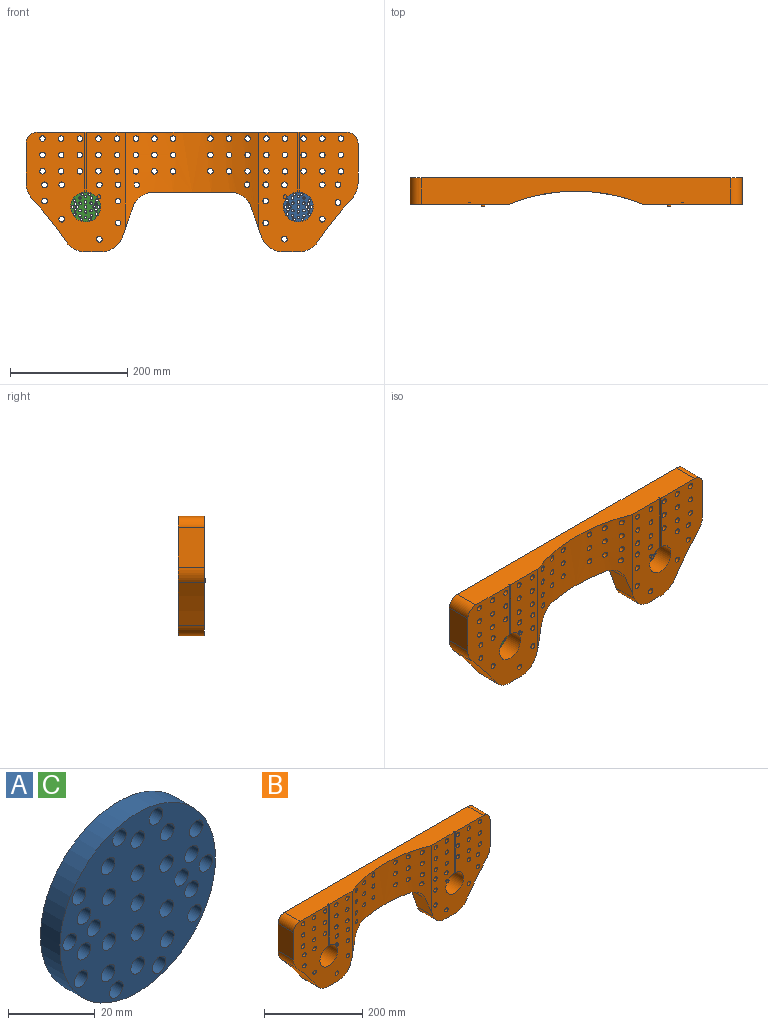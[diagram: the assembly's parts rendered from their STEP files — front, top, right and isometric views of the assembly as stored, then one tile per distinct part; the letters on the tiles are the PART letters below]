
ASSEMBLY  parts=3 mates=2
PART A: 32 faces, bbox 50.8x6.4x50.8 mm
  f0: cylinder r=2.22mm len=6.35mm, axis (0,1,0), area 88.7mm2, adj f30,f31
  f1: cylinder r=2.22mm len=6.35mm, axis (0,1,0), area 88.7mm2, adj f30,f31
  f2: cylinder r=2.22mm len=6.35mm, axis (0,1,0), area 88.7mm2, adj f30,f31
  f3: cylinder r=2.22mm len=6.35mm, axis (0,1,0), area 88.7mm2, adj f30,f31
  f4: cylinder r=2.22mm len=6.35mm, axis (0,1,0), area 88.7mm2, adj f30,f31
  f5: cylinder r=2.22mm len=6.35mm, axis (0,1,0), area 88.7mm2, adj f30,f31
  f6: cylinder r=2.22mm len=6.35mm, axis (0,1,0), area 88.7mm2, adj f30,f31
  f7: cylinder r=2.22mm len=6.35mm, axis (0,1,0), area 88.7mm2, adj f30,f31
  f8: cylinder r=2.22mm len=6.35mm, axis (0,1,0), area 88.7mm2, adj f30,f31
  f9: cylinder r=2.22mm len=6.35mm, axis (0,1,0), area 88.7mm2, adj f30,f31
  f10: cylinder r=2.22mm len=6.35mm, axis (0,1,0), area 88.7mm2, adj f30,f31
  f11: cylinder r=2.22mm len=6.35mm, axis (0,1,0), area 88.7mm2, adj f30,f31
  f12: cylinder r=2.22mm len=6.35mm, axis (0,1,0), area 88.7mm2, adj f30,f31
  f13: cylinder r=2.22mm len=6.35mm, axis (0,1,0), area 88.7mm2, adj f30,f31
  f14: cylinder r=2.22mm len=6.35mm, axis (0,1,0), area 88.7mm2, adj f30,f31
  f15: cylinder r=2.22mm len=6.35mm, axis (0,1,0), area 88.7mm2, adj f30,f31
  f16: cylinder r=2.22mm len=6.35mm, axis (0,1,0), area 88.7mm2, adj f30,f31
  f17: cylinder r=2.22mm len=6.35mm, axis (0,1,0), area 88.7mm2, adj f30,f31
  f18: cylinder r=25.4mm len=50.8mm, axis (0,1,0), area 1013.4mm2, adj f30,f31
  f19: cylinder r=2.22mm len=6.35mm, axis (0,1,0), area 88.7mm2, adj f30,f31
  f20: cylinder r=2.22mm len=6.35mm, axis (0,1,0), area 88.7mm2, adj f30,f31
  f21: cylinder r=2.22mm len=6.35mm, axis (0,1,0), area 88.7mm2, adj f30,f31
  f22: cylinder r=2.22mm len=6.35mm, axis (0,1,0), area 88.7mm2, adj f30,f31
  f23: cylinder r=2.22mm len=6.35mm, axis (0,1,0), area 88.7mm2, adj f30,f31
  f24: cylinder r=2.22mm len=6.35mm, axis (0,1,0), area 88.7mm2, adj f30,f31
  f25: cylinder r=2.22mm len=6.35mm, axis (0,1,0), area 88.7mm2, adj f30,f31
  f26: cylinder r=2.22mm len=6.35mm, axis (0,1,0), area 88.7mm2, adj f30,f31
  f27: cylinder r=2.22mm len=6.35mm, axis (0,1,0), area 88.7mm2, adj f30,f31
  f28: cylinder r=2.22mm len=6.35mm, axis (0,1,0), area 88.7mm2, adj f30,f31
  f29: cylinder r=2.22mm len=6.35mm, axis (0,1,0), area 88.7mm2, adj f30,f31
  f30: plane 50.8x50.8mm, normal (0,-1,0), area 1576.8mm2, adj f0,f1,f2,f3,f4,f5,f6,f7
  f31: plane 50.8x50.8mm, normal (0,1,0), area 1576.8mm2, adj f0,f1,f2,f3,f4,f5,f6,f7
PART B: 110 faces, bbox 565.2x47.6x203.2 mm
  f0: plane 203.2x168.71mm, normal (0,-1,0), area 25330.4mm2, adj f2,f4,f6,f7,f8,f9,f10,f11
  f1: plane 203.2x168.71mm, normal (0,-1,0), area 25330.4mm2, adj f2,f3,f4,f12,f13,f14,f15,f16
  f2: plane 527.05x44.45mm, normal (0,0,1), area 20014.2mm2, adj f0,f1,f4,f5,f11,f12,f98,f99
  f3: cylinder r=25.4mm len=50.8mm, axis (0,1,0), area 6070.4mm2, adj f1,f28,f98,f99,f100,f104
  f4: cylinder r=303.37mm len=227.74mm, axis (0,0,-1), area 24015.6mm2, adj f0,f1,f2,f19,f20,f21,f22,f23
  f5: plane 565.15x203.2mm, normal (0,1,0), area 69669.2mm2, adj f2,f6,f7,f8,f9,f10,f11,f12
  f6: plane 44.45x28.44mm, normal (0,0,-1), area 1264mm2, adj f0,f5,f7,f25
  f7: cylinder r=38.1mm len=44.45mm, axis (0,1,0), area 1651.6mm2, adj f0,f5,f6,f8
  f8: cylinder r=659.08mm len=74.21mm, axis (0,1,0), area 4202.9mm2, adj f0,f5,f7,f9
  f9: cylinder r=38.1mm len=44.45mm, axis (0,1,0), area 1251.6mm2, adj f0,f5,f8,f10
  f10: plane 67.55x44.45mm, normal (1,0,0), area 3002.8mm2, adj f0,f5,f9,f11
  f11: cylinder r=19.05mm len=44.45mm, axis (0,1,0), area 1330.1mm2, adj f0,f2,f5,f10
  f12: cylinder r=19.05mm len=44.45mm, axis (0,1,0), area 1330.1mm2, adj f1,f2,f5,f13
  f13: plane 67.55x44.45mm, normal (-1,0,0), area 3002.8mm2, adj f1,f5,f12,f14
  f14: cylinder r=38.1mm len=44.45mm, axis (0,1,0), area 1251.6mm2, adj f1,f5,f13,f15
  f15: cylinder r=659.08mm len=74.21mm, axis (0,1,0), area 4202.9mm2, adj f1,f5,f14,f16
  f16: cylinder r=38.1mm len=44.45mm, axis (0,1,0), area 1651.6mm2, adj f1,f5,f15,f17
  f17: plane 44.45x28.44mm, normal (0,0,-1), area 1264mm2, adj f1,f5,f16,f18
  f18: cylinder r=38.1mm len=44.45mm, axis (0,1,0), area 2099.5mm2, adj f1,f5,f17,f19
  f19: plane 50.17x44.45mm, normal (0.95,0,-0.33), area 2258.2mm2, adj f1,f4,f5,f18,f20
  f20: cylinder r=38.1mm len=39.55mm, axis (0,1,0), area 1644.6mm2, adj f4,f5,f19,f21
  f21: plane 129.77x29.29mm, normal (0,0,-1), area 3192mm2, adj f4,f5,f20,f22
  f22: cylinder r=38.1mm len=39.55mm, axis (0,1,0), area 1644.6mm2, adj f4,f5,f21,f23
  f23: plane 50.17x44.45mm, normal (-0.95,0,-0.33), area 2258.2mm2, adj f0,f4,f5,f22,f25
  f24: cylinder r=25.4mm len=50.8mm, axis (0,1,0), area 6070.4mm2, adj f0,f27,f101,f102,f103,f107
  f25: cylinder r=38.1mm len=44.45mm, axis (0,1,0), area 2099.5mm2, adj f0,f5,f6,f23
  f26: cylinder r=38.1mm len=76.2mm, axis (0,1,0), area 1520.1mm2, adj f5,f27
  f27: plane 76.2x76.2mm, normal (0,1,0), area 2533.5mm2, adj f24,f26
  f28: plane 76.2x76.2mm, normal (0,1,0), area 2533.5mm2, adj f3,f29
  f29: cylinder r=38.1mm len=76.2mm, axis (0,1,0), area 1520.1mm2, adj f5,f28
  f30: cylinder r=4.76mm len=24.42mm, axis (0,1,0), area 715.4mm2, adj f4,f5
  f31: cylinder r=4.76mm len=24.53mm, axis (0,1,0), area 718.2mm2, adj f4,f5
  f32: cylinder r=4.76mm len=29.94mm, axis (0,1,0), area 865.1mm2, adj f4,f5
  f33: cylinder r=4.76mm len=24.42mm, axis (0,1,0), area 715.4mm2, adj f4,f5
  f34: cylinder r=4.76mm len=24.53mm, axis (0,1,0), area 718.2mm2, adj f4,f5
  f35: cylinder r=4.76mm len=24.53mm, axis (0,1,0), area 718.2mm2, adj f4,f5
  f36: cylinder r=4.76mm len=24.42mm, axis (0,1,0), area 715.4mm2, adj f4,f5
  f37: cylinder r=4.76mm len=29.94mm, axis (0,1,0), area 865.1mm2, adj f4,f5
  f38: cylinder r=4.76mm len=30.16mm, axis (0,1,0), area 871mm2, adj f4,f5
  f39: cylinder r=4.76mm len=29.94mm, axis (0,1,0), area 865.1mm2, adj f4,f5
  f40: cylinder r=4.76mm len=30.16mm, axis (0,1,0), area 871mm2, adj f4,f5
  f41: cylinder r=4.76mm len=30.16mm, axis (0,1,0), area 871mm2, adj f4,f5
  f42: cylinder r=4.76mm len=38.74mm, axis (0,1,0), area 1112.2mm2, adj f4,f5
  f43: cylinder r=4.76mm len=38.85mm, axis (0,1,0), area 1115.2mm2, adj f4,f5
  f44: cylinder r=4.76mm len=39.39mm, axis (0,1,0), area 1130.6mm2, adj f4,f5
  f45: cylinder r=4.76mm len=39.39mm, axis (0,1,0), area 1130.6mm2, adj f4,f5
  f46: cylinder r=4.76mm len=39.07mm, axis (0,1,0), area 1121.6mm2, adj f4,f5
  f47: cylinder r=4.76mm len=39.07mm, axis (0,1,0), area 1121.6mm2, adj f4,f5
  f48: cylinder r=4.76mm len=39.07mm, axis (0,1,0), area 1121.6mm2, adj f4,f5
  f49: cylinder r=4.76mm len=39.39mm, axis (0,1,0), area 1130.6mm2, adj f4,f5
  f50: cylinder r=4.76mm len=44.45mm, axis (0,1,0), area 1330.1mm2, adj f1,f5
  f51: cylinder r=4.76mm len=44.45mm, axis (0,1,0), area 1330.1mm2, adj f1,f5
  f52: cylinder r=4.76mm len=44.45mm, axis (0,1,0), area 1330.1mm2, adj f1,f5
  f53: cylinder r=4.76mm len=44.45mm, axis (0,1,0), area 1330.1mm2, adj f1,f5
  f54: cylinder r=4.76mm len=44.45mm, axis (0,1,0), area 1330.1mm2, adj f1,f5
  f55: cylinder r=4.76mm len=44.45mm, axis (0,1,0), area 1330.1mm2, adj f1,f5
  f56: cylinder r=4.76mm len=44.45mm, axis (0,1,0), area 1330.1mm2, adj f1,f5
  f57: cylinder r=4.76mm len=44.45mm, axis (0,1,0), area 1330.1mm2, adj f1,f5
  f58: cylinder r=4.76mm len=44.45mm, axis (0,1,0), area 1330.1mm2, adj f1,f5
  f59: cylinder r=4.76mm len=44.45mm, axis (0,1,0), area 1330.1mm2, adj f1,f5
  f60: cylinder r=4.76mm len=44.45mm, axis (0,1,0), area 1330.1mm2, adj f1,f5
  f61: cylinder r=4.76mm len=44.45mm, axis (0,1,0), area 1330.1mm2, adj f1,f5
  f62: cylinder r=4.76mm len=44.45mm, axis (0,1,0), area 1330.1mm2, adj f1,f5
  f63: cylinder r=4.76mm len=44.45mm, axis (0,1,0), area 1330.1mm2, adj f1,f5
  f64: cylinder r=4.76mm len=44.45mm, axis (0,1,0), area 1330.1mm2, adj f1,f5
  f65: cylinder r=4.76mm len=44.45mm, axis (0,1,0), area 1330.1mm2, adj f1,f5
  f66: cylinder r=4.76mm len=44.45mm, axis (0,1,0), area 1330.1mm2, adj f1,f5
  f67: cylinder r=4.76mm len=44.45mm, axis (0,1,0), area 1330.1mm2, adj f1,f5
  f68: cylinder r=4.76mm len=44.45mm, axis (0,1,0), area 1330.1mm2, adj f1,f5
  f69: cylinder r=4.76mm len=44.45mm, axis (0,1,0), area 1330.1mm2, adj f1,f5
  f70: cylinder r=4.76mm len=44.45mm, axis (0,1,0), area 1330.1mm2, adj f1,f5
  f71: cylinder r=4.76mm len=44.45mm, axis (0,1,0), area 1330.1mm2, adj f1,f5
  f72: cylinder r=4.76mm len=44.45mm, axis (0,1,0), area 1330.1mm2, adj f1,f5
  f73: cylinder r=4.76mm len=44.45mm, axis (0,1,0), area 1330.1mm2, adj f1,f5
  f74: cylinder r=4.76mm len=44.45mm, axis (0,1,0), area 1330.1mm2, adj f0,f5
  f75: cylinder r=4.76mm len=44.45mm, axis (0,1,0), area 1330.1mm2, adj f0,f5
  f76: cylinder r=4.76mm len=44.45mm, axis (0,1,0), area 1330.1mm2, adj f0,f5
  f77: cylinder r=4.76mm len=44.45mm, axis (0,1,0), area 1330.1mm2, adj f0,f5
  f78: cylinder r=4.76mm len=44.45mm, axis (0,1,0), area 1330.1mm2, adj f0,f5
  f79: cylinder r=4.76mm len=44.45mm, axis (0,1,0), area 1330.1mm2, adj f0,f5
  f80: cylinder r=4.76mm len=44.45mm, axis (0,1,0), area 1330.1mm2, adj f0,f5
  f81: cylinder r=4.76mm len=44.45mm, axis (0,1,0), area 1330.1mm2, adj f0,f5
  f82: cylinder r=4.76mm len=44.45mm, axis (0,1,0), area 1330.1mm2, adj f0,f5
  f83: cylinder r=4.76mm len=44.45mm, axis (0,1,0), area 1330.1mm2, adj f0,f5
  f84: cylinder r=4.76mm len=44.45mm, axis (0,1,0), area 1330.1mm2, adj f0,f5
  f85: cylinder r=4.76mm len=44.45mm, axis (0,1,0), area 1330.1mm2, adj f0,f5
  f86: cylinder r=4.76mm len=44.45mm, axis (0,1,0), area 1330.1mm2, adj f0,f5
  f87: cylinder r=4.76mm len=44.45mm, axis (0,1,0), area 1330.1mm2, adj f0,f5
  f88: cylinder r=4.76mm len=44.45mm, axis (0,1,0), area 1330.1mm2, adj f0,f5
  f89: cylinder r=4.76mm len=44.45mm, axis (0,1,0), area 1330.1mm2, adj f0,f5
  f90: cylinder r=4.76mm len=44.45mm, axis (0,1,0), area 1330.1mm2, adj f0,f5
  f91: cylinder r=4.76mm len=44.45mm, axis (0,1,0), area 1330.1mm2, adj f0,f5
  f92: cylinder r=4.76mm len=44.45mm, axis (0,1,0), area 1330.1mm2, adj f0,f5
  f93: cylinder r=4.76mm len=44.45mm, axis (0,1,0), area 1330.1mm2, adj f0,f5
  f94: cylinder r=4.76mm len=44.45mm, axis (0,1,0), area 1330.1mm2, adj f0,f5
  f95: cylinder r=4.76mm len=44.45mm, axis (0,1,0), area 1330.1mm2, adj f0,f5
  f96: cylinder r=4.76mm len=44.45mm, axis (0,1,0), area 1330.1mm2, adj f0,f5
  f97: cylinder r=4.76mm len=44.45mm, axis (0,1,0), area 1330.1mm2, adj f0,f5
  f98: plane 101.65x3.18mm, normal (0,-1,0), area 322.6mm2, adj f2,f3,f99,f100
  f99: plane 101.65x3.18mm, normal (-1,0,0), area 322.7mm2, adj f1,f2,f3,f98
  f100: plane 101.65x3.18mm, normal (1,0,0), area 322.7mm2, adj f1,f2,f3,f98
  f101: plane 101.65x3.18mm, normal (1,0,0), area 322.7mm2, adj f0,f2,f24,f103
  f102: plane 101.65x3.18mm, normal (-1,0,0), area 322.7mm2, adj f0,f2,f24,f103
  f103: plane 101.65x3.18mm, normal (0,-1,0), area 322.6mm2, adj f2,f24,f101,f102
  f104: plane 0.98x0.76mm, normal (0,1,0), area 0.1mm2, adj f3,f105
  f105: cylinder r=3.17mm len=6.35mm, axis (0,1,0), area 63.3mm2, adj f1,f104,f106
  f106: plane 6.35x6.35mm, normal (0,-1,0), area 31.7mm2, adj f105
  f107: plane 0.98x0.76mm, normal (0,1,0), area 0.1mm2, adj f24,f108
  f108: cylinder r=3.17mm len=6.35mm, axis (0,1,0), area 63.3mm2, adj f0,f107,f109
  f109: plane 6.35x6.35mm, normal (0,-1,0), area 31.7mm2, adj f108
PART C: same geometry as A
PLACE A t=(142.39,7.83,-84.73)mm
PLACE B t=(-38.58,14.18,-59.33)mm
PLACE C t=(-219.56,7.83,-84.73)mm
MATE fastened C.f18 <-> B.f3  axis (0,1,0) through (-219.56,7.83,-84.73)mm
MATE fastened A.f18 <-> B.f24  axis (0,1,0) through (142.39,7.83,-84.73)mm
